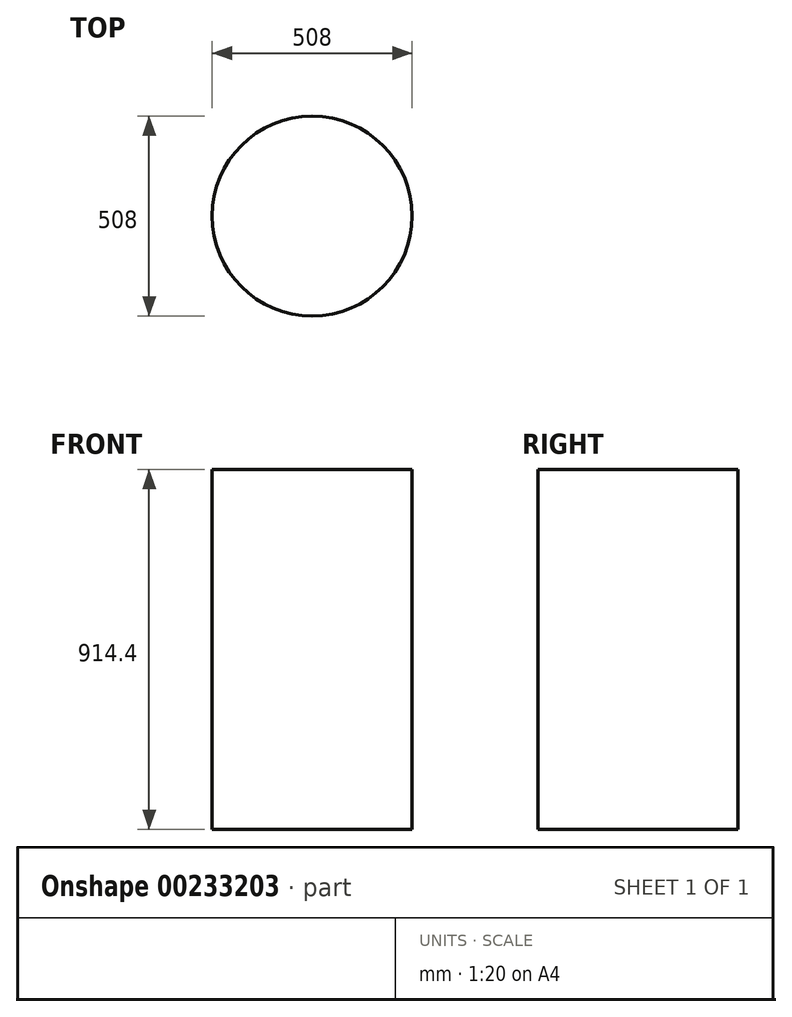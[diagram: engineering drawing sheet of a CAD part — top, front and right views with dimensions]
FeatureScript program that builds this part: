
annotation { "Feature Type Name" : "Feature", "Feature Type Description" : "" }
export const myFeature = defineFeature(function(context is Context, id is Id, definition is map)
    precondition{}
    {
        {
            var Q0;
            Q0=qCreatedBy(makeId("Top.planeOp"),FACE);
            var sketch = newSketch(context, id + "F0", { "sketchPlane" : qUnion([Q0])});
            skCircle(sketch, "E0", {"center": v(-4.88, 17.32) * mm, "radius": 254 * mm});
            skSolve(sketch);
        }
        {
            var Q0;
            Q0 = qSketchRegion(id + "F0", true);
            extrude(context, id + "F1", {"entities" : qUnion([Q0]), "depth" : 914.4 * mm});
        }
    });
